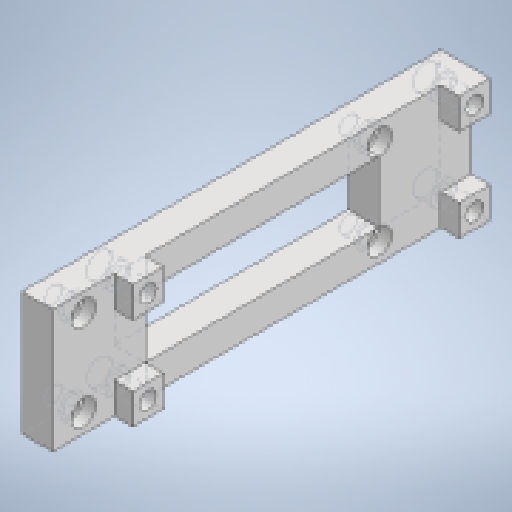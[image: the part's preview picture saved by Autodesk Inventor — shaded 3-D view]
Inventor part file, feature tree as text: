
AUTODESK INVENTOR PART (.ipt)
format: ipt  version: 2023 (Build 270158000, 158)  size: 328,192 bytes
history: native  units: mm
features: extrude x11, sketch x11, projected_geometry x2
ambient origin geometry x8: Origin, YZ Plane, XZ Plane, XY Plane, X Axis, Y Axis, Z Axis, Center Point
bodies: Solid1 (feature_tree)
feature tree (24):
  extrude  "Extrusion1"  Depth=5.0mm
  extrude  "Extrusion2"  Depth=15.0mm
  extrude  "Extrusion3"  Depth=48.0mm
  extrude  "Extrusion4"  Depth=10.0mm
  extrude  "Extrusion5"  Depth=10.0mm
  extrude  "Extrusion6"  Depth=5.0mm TaperAngle=0.0deg
  extrude  "Extrusion7"  Depth=5.0mm
  extrude  "Extrusion8"  Depth=10.0mm
  extrude  "Extrusion9"  Depth=3.0mm
  extrude  "Extrusion10"  Depth=5.0mm
  extrude  "Extrusion11"  Depth=5.0mm
  sketch  "Sketch1"  dims[d0=5.0mm d1=5.0mm]
  sketch  "Sketch2"  dims[d2=5.0mm d3=15.0mm]
  sketch  "Sketch3"  dims[d4=15.0mm d5=48.0mm]
  sketch  "Sketch4"  dims[d6=20.0mm d7=0.0mm d8=10.0mm]
  sketch  "Sketch5"  dims[d9=10.0mm d10=10.0mm]
  sketch  "Sketch6"  dims[d11=5.0mm d12=200.0mm d13=0.0mm]
  sketch  "Sketch7"  dims[d14=5.0mm d15=5.0mm]
  projected_geometry  "Projected Loop1"
  sketch  "Sketch8"  dims[d16=20.0mm d17=0.0mm d18=10.0mm]
  projected_geometry  "Projected Loop2"
  sketch  "Sketch9"  dims[d19=10.0mm d20=3.0mm]
  sketch  "Sketch10"  dims[d21=3.0mm d22=5.0mm]
  sketch  "Sketch11"  dims[d23=5.0mm d24=5.0mm d25=5.0mm d26=3.0mm d27=3.0mm d28=2.75mm d29=2.75mm d30=2.75mm d31=2.75mm d32=5.0mm d33=0.0mm d34=2.5mm d35=2.5mm d36=2.5mm d37=2.5mm d38=2.5mm d39=2.5mm d40=2.5mm d41=2.5mm d42=2.75mm d43=2.75mm d44=2.75mm d45=2.75mm d46=15.0mm d47=0.0mm d48=4.0mm d49=4.0mm d50=4.0mm d51=4.0mm d52=3.0mm d53=0.0mm d54=12.0mm d55=4.0mm d56=3.0mm d57=5.0mm d58=5.0mm d59=3.0mm d60=3.0mm d61=1000.0mm d62=0.0mm d63=0.0mm d64=0.0mm d65=10.0mm d66=5.0mm d67=0.0mm d68=5.0mm d69=3.0mm d70=3.0mm d71=3.0mm d72=5.0mm d73=5.0mm d74=2.75mm d75=2.75mm d76=2.75mm d77=5.0mm d78=0.0mm d79=5.0mm d80=5.0mm d81=0.0mm d82=4.0mm d83=4.0mm d84=4.0mm d85=4.0mm d86=2.0mm d87=0.0mm]
